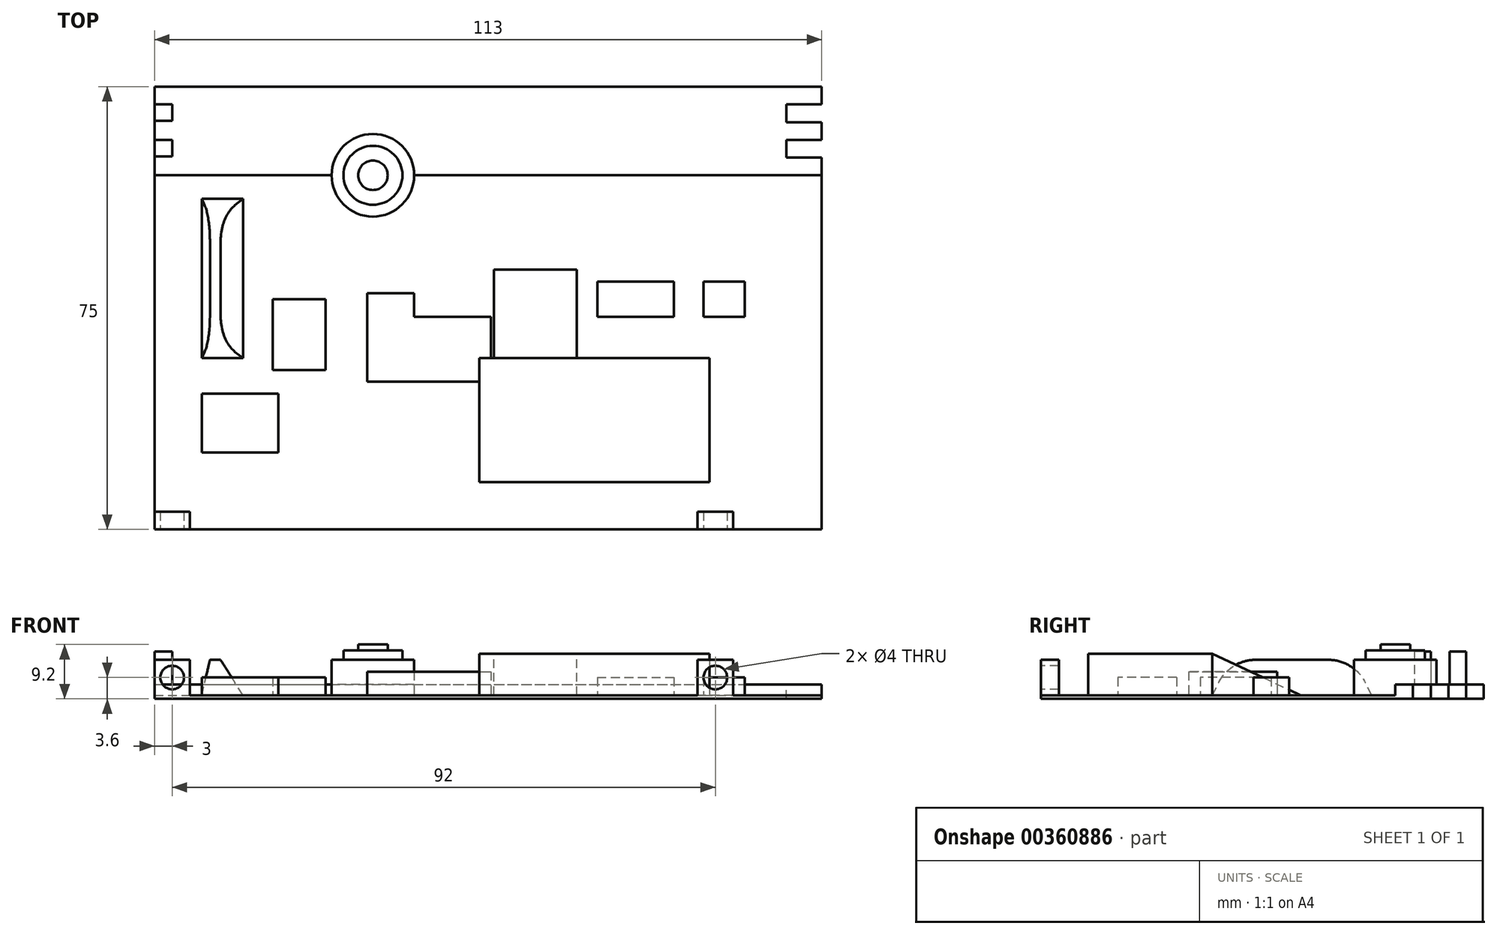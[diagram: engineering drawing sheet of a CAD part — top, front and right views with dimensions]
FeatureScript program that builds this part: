
annotation { "Feature Type Name" : "Feature", "Feature Type Description" : "" }
export const myFeature = defineFeature(function(context is Context, id is Id, definition is map)
    precondition{}
    {
        {
            var Q0;
            Q0=qCreatedBy(makeId("Top.planeOp"),FACE);
            var sketch = newSketch(context, id + "F0", { "sketchPlane" : qUnion([Q0])});
            skLineSegment(sketch, "E0.bottom", {"start": v(-56.5, 75) * mm, "end": v(56.5, 75) * mm});
            skLineSegment(sketch, "E0.top", {"start": v(-56.5, 0) * mm, "end": v(56.5, 0) * mm});
            skLineSegment(sketch, "E0.left", {"start": v(-56.5, 75) * mm, "end": v(-56.5, 0) * mm});
            skLineSegment(sketch, "E0.right", {"start": v(56.5, 75) * mm, "end": v(56.5, 0) * mm});
            skPoint(sketch, "E1", {"position": v(0, 0) * mm});
            skSolve(sketch);
        }
        {
            var Q0;
            Q0 = qSketchRegion(id + "F0", true);
            extrude(context, id + "F1", {"entities" : qUnion([Q0]), "depth" : 0.6 * mm});
        }
        {
            var Q0;
            Q0=makeQuery(id+"F1.opExtrude","CAP_FACE",FACE,{"disambiguationData":[OSD([sQuery(id+"F0.wireOp",EDGE,"E0.bottom"),sQuery(id+"F0.wireOp",EDGE,"E0.top"),sQuery(id+"F0.wireOp",EDGE,"E0.left"),sQuery(id+"F0.wireOp",EDGE,"E0.right")])],"isStart":false});
            var sketch = newSketch(context, id + "F2", { "sketchPlane" : qUnion([Q0])});
            skLineSegment(sketch, "E2.bottom", {"start": v(-56.5, 75) * mm, "end": v(56.5, 75) * mm});
            skLineSegment(sketch, "E2.top", {"start": v(-56.5, 60) * mm, "end": v(56.5, 60) * mm});
            skLineSegment(sketch, "E2.left", {"start": v(-56.5, 75) * mm, "end": v(-56.5, 60) * mm});
            skLineSegment(sketch, "E2.right", {"start": v(56.5, 75) * mm, "end": v(56.5, 60) * mm});
            skSolve(sketch);
        }
        {
            var Q0;
            Q0 = qSketchRegion(id + "F2", true);
            extrude(context, id + "F3", {"entities" : qUnion([Q0]), "operationType" : NewBodyOperationType.ADD, "depth" : 1.8 * mm});
        }
        {
            var Q0;
            Q0=makeQuery(id+"F1.opExtrude","CAP_FACE",FACE,{"disambiguationData":[OSD([sQuery(id+"F0.wireOp",EDGE,"E0.bottom"),sQuery(id+"F0.wireOp",EDGE,"E0.top"),sQuery(id+"F0.wireOp",EDGE,"E0.left"),sQuery(id+"F0.wireOp",EDGE,"E0.right")])],"isStart":false});
            var sketch = newSketch(context, id + "F4", { "sketchPlane" : qUnion([Q0])});
            skCircle(sketch, "E3", {"center": v(-19.5, 60) * mm, "radius": 7 * mm});
            skSolve(sketch);
        }
        {
            var Q0;
            Q0 = qSketchRegion(id + "F4", true);
            extrude(context, id + "F5", {"entities" : qUnion([Q0]), "operationType" : NewBodyOperationType.ADD, "depth" : 6 * mm});
        }
        {
            var Q0;
            Q0=makeQuery(id+"F5.opExtrude","CAP_FACE",FACE,{"disambiguationData":[OSD([sQuery(id+"F4.wireOp",EDGE,"E3")])],"isStart":false});
            var sketch = newSketch(context, id + "F6", { "sketchPlane" : qUnion([Q0])});
            skCircle(sketch, "E4", {"center": v(-19.5, 60) * mm, "radius": 5 * mm});
            skSolve(sketch);
        }
        {
            var Q0;
            Q0 = qSketchRegion(id + "F6", true);
            extrude(context, id + "F7", {"entities" : qUnion([Q0]), "operationType" : NewBodyOperationType.ADD, "depth" : 1.6 * mm});
        }
        {
            var Q0;
            Q0=makeQuery(id+"F7.opExtrude","CAP_FACE",FACE,{"disambiguationData":[OSD([sQuery(id+"F6.wireOp",EDGE,"E4")])],"isStart":false});
            var sketch = newSketch(context, id + "F8", { "sketchPlane" : qUnion([Q0])});
            skCircle(sketch, "E5", {"center": v(-19.5, 60) * mm, "radius": 2.5 * mm});
            skSolve(sketch);
        }
        {
            var Q0;
            Q0 = qSketchRegion(id + "F8", true);
            extrude(context, id + "F9", {"entities" : qUnion([Q0]), "operationType" : NewBodyOperationType.ADD, "depth" : 1 * mm});
        }
        {
            var Q0;
            Q0=makeQuery(id+"F1.opExtrude","CAP_FACE",FACE,{"disambiguationData":[OSD([sQuery(id+"F0.wireOp",EDGE,"E0.bottom"),sQuery(id+"F0.wireOp",EDGE,"E0.top"),sQuery(id+"F0.wireOp",EDGE,"E0.left"),sQuery(id+"F0.wireOp",EDGE,"E0.right")])],"isStart":false});
            var sketch = newSketch(context, id + "F10", { "sketchPlane" : qUnion([Q0])});
            skLineSegment(sketch, "E6.bottom", {"start": v(-48.5, 23) * mm, "end": v(-35.5, 23) * mm});
            skLineSegment(sketch, "E6.top", {"start": v(-48.5, 13) * mm, "end": v(-35.5, 13) * mm});
            skLineSegment(sketch, "E6.left", {"start": v(-48.5, 23) * mm, "end": v(-48.5, 13) * mm});
            skLineSegment(sketch, "E6.right", {"start": v(-35.5, 23) * mm, "end": v(-35.5, 13) * mm});
            skLineSegment(sketch, "E7.bottom", {"start": v(-36.5, 39) * mm, "end": v(-27.5, 39) * mm});
            skLineSegment(sketch, "E7.top", {"start": v(-36.5, 27) * mm, "end": v(-27.5, 27) * mm});
            skLineSegment(sketch, "E7.left", {"start": v(-36.5, 39) * mm, "end": v(-36.5, 27) * mm});
            skLineSegment(sketch, "E7.right", {"start": v(-27.5, 39) * mm, "end": v(-27.5, 27) * mm});
            skLineSegment(sketch, "E8.bottom", {"start": v(18.5, 42) * mm, "end": v(31.5, 42) * mm});
            skLineSegment(sketch, "E8.top", {"start": v(18.5, 36) * mm, "end": v(31.5, 36) * mm});
            skLineSegment(sketch, "E8.left", {"start": v(18.5, 42) * mm, "end": v(18.5, 36) * mm});
            skLineSegment(sketch, "E8.right", {"start": v(31.5, 42) * mm, "end": v(31.5, 36) * mm});
            skLineSegment(sketch, "E9.bottom", {"start": v(36.5, 42) * mm, "end": v(43.5, 42) * mm});
            skLineSegment(sketch, "E9.top", {"start": v(36.5, 36) * mm, "end": v(43.5, 36) * mm});
            skLineSegment(sketch, "E9.left", {"start": v(36.5, 42) * mm, "end": v(36.5, 36) * mm});
            skLineSegment(sketch, "E9.right", {"start": v(43.5, 42) * mm, "end": v(43.5, 36) * mm});
            skSolve(sketch);
        }
        {
            var Q0;
            Q0 = qSketchRegion(id + "F10", true);
            extrude(context, id + "F11", {"entities" : qUnion([Q0]), "operationType" : NewBodyOperationType.ADD, "depth" : 3 * mm});
        }
        {
            var Q0;
            Q0=makeQuery(id+"F1.opExtrude","CAP_FACE",FACE,{"disambiguationData":[OSD([sQuery(id+"F0.wireOp",EDGE,"E0.bottom"),sQuery(id+"F0.wireOp",EDGE,"E0.top"),sQuery(id+"F0.wireOp",EDGE,"E0.left"),sQuery(id+"F0.wireOp",EDGE,"E0.right")])],"isStart":false});
            var sketch = newSketch(context, id + "F12", { "sketchPlane" : qUnion([Q0])});
            skLineSegment(sketch, "E10", {"start": v(-20.5, 40) * mm, "end": v(-12.5, 40) * mm});
            skLineSegment(sketch, "E11", {"start": v(-12.5, 40) * mm, "end": v(-12.5, 36) * mm});
            skLineSegment(sketch, "E12", {"start": v(-12.5, 36) * mm, "end": v(0.5, 36) * mm});
            skLineSegment(sketch, "E13", {"start": v(0.5, 36) * mm, "end": v(0.5, 25) * mm});
            skLineSegment(sketch, "E14", {"start": v(0.5, 25) * mm, "end": v(-20.5, 25) * mm});
            skLineSegment(sketch, "E15", {"start": v(-20.5, 25) * mm, "end": v(-20.5, 40) * mm});
            skSolve(sketch);
        }
        {
            var Q0;
            Q0=makeQuery(id+"F1.opExtrude","CAP_FACE",FACE,{"disambiguationData":[OSD([sQuery(id+"F0.wireOp",EDGE,"E0.bottom"),sQuery(id+"F0.wireOp",EDGE,"E0.top"),sQuery(id+"F0.wireOp",EDGE,"E0.left"),sQuery(id+"F0.wireOp",EDGE,"E0.right")])],"isStart":false});
            var sketch = newSketch(context, id + "F13", { "sketchPlane" : qUnion([Q0])});
            skLineSegment(sketch, "E16.bottom", {"start": v(-1.5, 29) * mm, "end": v(37.5, 29) * mm});
            skLineSegment(sketch, "E16.top", {"start": v(-1.5, 8) * mm, "end": v(37.5, 8) * mm});
            skLineSegment(sketch, "E16.left", {"start": v(-1.5, 29) * mm, "end": v(-1.5, 8) * mm});
            skLineSegment(sketch, "E16.right", {"start": v(37.5, 29) * mm, "end": v(37.5, 8) * mm});
            skSolve(sketch);
        }
        {
            var Q0;
            Q0 = qSketchRegion(id + "F13", true);
            extrude(context, id + "F14", {"entities" : qUnion([Q0]), "operationType" : NewBodyOperationType.ADD, "depth" : 7 * mm});
        }
        {
            var Q0;
            Q0 = qSketchRegion(id + "F12", true);
            extrude(context, id + "F15", {"entities" : qUnion([Q0]), "operationType" : NewBodyOperationType.ADD, "depth" : 4 * mm});
        }
        {
            var Q0;
            Q0=qCreatedBy(makeId("Right.planeOp"),FACE);
            cPlane(context, id + "F16", {"entities" : qUnion([Q0]), "cplaneType" : CPlaneType.OFFSET, "offset" : 15 * mm, "width" : 150 * mm, "height" : 150 * mm});
        }
        {
            var Q0;
            Q0=qCreatedBy(id+"F16.planeOp",FACE);
            var sketch = newSketch(context, id + "F17", { "sketchPlane" : qUnion([Q0])});
            skLineSegment(sketch, "E17", {"start": v(44, 0.6) * mm, "end": v(29, 0.6) * mm});
            skLineSegment(sketch, "E18", {"start": v(29, 0.6) * mm, "end": v(29, 7.6) * mm});
            skLineSegment(sketch, "E19", {"start": v(29, 7.6) * mm, "end": v(44, 0.6) * mm});
            skSolve(sketch);
        }
        {
            var Q0;
            Q0 = qSketchRegion(id + "F17", true);
            extrude(context, id + "F18", {"entities" : qUnion([Q0]), "operationType" : NewBodyOperationType.ADD, "oppositeDirection" : true, "depth" : 14 * mm});
        }
        {
            var Q0;
            Q0=makeQuery(id+"F1.opExtrude","CAP_FACE",FACE,{"disambiguationData":[OSD([sQuery(id+"F0.wireOp",EDGE,"E0.bottom"),sQuery(id+"F0.wireOp",EDGE,"E0.top"),sQuery(id+"F0.wireOp",EDGE,"E0.left"),sQuery(id+"F0.wireOp",EDGE,"E0.right")])],"isStart":false});
            var sketch = newSketch(context, id + "F19", { "sketchPlane" : qUnion([Q0])});
            skLineSegment(sketch, "E20.bottom", {"start": v(-48.5, 56) * mm, "end": v(-41.5, 56) * mm});
            skLineSegment(sketch, "E20.top", {"start": v(-48.5, 29) * mm, "end": v(-41.5, 29) * mm});
            skLineSegment(sketch, "E20.left", {"start": v(-48.5, 56) * mm, "end": v(-48.5, 29) * mm});
            skLineSegment(sketch, "E20.right", {"start": v(-41.5, 56) * mm, "end": v(-41.5, 29) * mm});
            skSolve(sketch);
        }
        {
            var Q0;
            Q0=makeQuery(id+"F19.imprint","IMPRINT",FACE,{"disambiguationData":[TD([[makeQuery(id+"F19.imprint","IMPRINT",EDGE,{"derivedFrom":sQuery(id+"F19.wireOp",EDGE,"E20.bottom")}),-1.0]])]});
            cPlane(context, id + "F20", {"entities" : qUnion([Q0]), "cplaneType" : CPlaneType.OFFSET, "offset" : 6 * mm, "width" : 150 * mm, "height" : 150 * mm});
        }
        {
            var Q0;
            Q0=qCreatedBy(id+"F20.planeOp",FACE);
            var sketch = newSketch(context, id + "F21", { "sketchPlane" : qUnion([Q0])});
            skLineSegment(sketch, "E21.bottom", {"start": v(-47.1, 53) * mm, "end": v(-45.3, 53) * mm});
            skLineSegment(sketch, "E21.top", {"start": v(-47.1, 32) * mm, "end": v(-45.3, 32) * mm});
            skLineSegment(sketch, "E21.left", {"start": v(-47.1, 53) * mm, "end": v(-47.1, 32) * mm});
            skLineSegment(sketch, "E21.right", {"start": v(-45.3, 53) * mm, "end": v(-45.3, 32) * mm});
            skSolve(sketch);
        }
        {
            var Q1;
            Q1=makeQuery(id+"F19.imprint","IMPRINT",FACE,{"disambiguationData":[TD([[makeQuery(id+"F19.imprint","IMPRINT",EDGE,{"derivedFrom":sQuery(id+"F19.wireOp",EDGE,"E20.bottom")}),-1.0]])]});
            var Q2;
            Q2=makeQuery(id+"F21.imprint","IMPRINT",FACE,{"disambiguationData":[TD([[makeQuery(id+"F21.imprint","IMPRINT",EDGE,{"derivedFrom":sQuery(id+"F21.wireOp",EDGE,"E21.bottom")}),-1.0]])]});
            loft(context, id + "F22", {"operationType" : NewBodyOperationType.ADD, "sheetProfilesArray" : [{ "sheetProfileEntities" : qUnion([Q1]) }, { "sheetProfileEntities" : qUnion([Q2]) }]});
        }
        {
            var Q0;
            Q0=makeQuery(id+"F22.opLoft","MID_CAP_EDGE",EDGE,{"disambiguationData":[OSD([sQuery(id+"F21.wireOp",EDGE,"E21.bottom"),sQuery(id+"F21.wireOp",EDGE,"E21.left"),sQuery(id+"F21.wireOp",EDGE,"E21.right")])],"capPos":1.0});
            var Q1;
            Q1=makeQuery(id+"F22.opLoft","MID_CAP_EDGE",EDGE,{"disambiguationData":[OSD([sQuery(id+"F21.wireOp",EDGE,"E21.top"),sQuery(id+"F21.wireOp",EDGE,"E21.left"),sQuery(id+"F21.wireOp",EDGE,"E21.right")])],"capPos":1.0});
            fillet(context, id + "F23", {"entities" : qUnion([Q0, Q1]), "radius" : 7 * mm, "tangentPropagation" : true, "allowEdgeOverflow" : false});
        }
        {
            var Q0;
            Q0=makeQuery(id+"F3.opExtrude","CAP_FACE",FACE,{"disambiguationData":[OSD([sQuery(id+"F2.wireOp",EDGE,"E2.bottom"),sQuery(id+"F2.wireOp",EDGE,"E2.top"),sQuery(id+"F2.wireOp",EDGE,"E2.left"),sQuery(id+"F2.wireOp",EDGE,"E2.right")])],"isStart":false});
            var sketch = newSketch(context, id + "F24", { "sketchPlane" : qUnion([Q0])});
            skLineSegment(sketch, "E22.bottom", {"start": v(-56.5, 72) * mm, "end": v(-53.5, 72) * mm});
            skLineSegment(sketch, "E22.top", {"start": v(-56.5, 69.2) * mm, "end": v(-53.5, 69.2) * mm});
            skLineSegment(sketch, "E22.left", {"start": v(-56.5, 72) * mm, "end": v(-56.5, 69.2) * mm});
            skLineSegment(sketch, "E22.right", {"start": v(-53.5, 72) * mm, "end": v(-53.5, 69.2) * mm});
            skLineSegment(sketch, "E23.bottom", {"start": v(-56.5, 66) * mm, "end": v(-53.5, 66) * mm});
            skLineSegment(sketch, "E23.top", {"start": v(-56.5, 63.2) * mm, "end": v(-53.5, 63.2) * mm});
            skLineSegment(sketch, "E23.left", {"start": v(-56.5, 66) * mm, "end": v(-56.5, 63.2) * mm});
            skLineSegment(sketch, "E23.right", {"start": v(-53.5, 66) * mm, "end": v(-53.5, 63.2) * mm});
            skSolve(sketch);
        }
        {
            var Q0;
            Q0 = qSketchRegion(id + "F24", true);
            extrude(context, id + "F25", {"entities" : qUnion([Q0]), "operationType" : NewBodyOperationType.ADD, "depth" : 5.6 * mm});
        }
        {
            var Q0;
            Q0=makeQuery(id+"F3.opExtrude","CAP_FACE",FACE,{"disambiguationData":[OSD([sQuery(id+"F2.wireOp",EDGE,"E2.bottom"),sQuery(id+"F2.wireOp",EDGE,"E2.top"),sQuery(id+"F2.wireOp",EDGE,"E2.left"),sQuery(id+"F2.wireOp",EDGE,"E2.right")])],"isStart":false});
            var sketch = newSketch(context, id + "F26", { "sketchPlane" : qUnion([Q0])});
            skLineSegment(sketch, "E24.bottom", {"start": v(50.5, 72) * mm, "end": v(56.5, 72) * mm});
            skLineSegment(sketch, "E24.top", {"start": v(50.5, 69) * mm, "end": v(56.5, 69) * mm});
            skLineSegment(sketch, "E24.left", {"start": v(50.5, 72) * mm, "end": v(50.5, 69) * mm});
            skLineSegment(sketch, "E24.right", {"start": v(56.5, 72) * mm, "end": v(56.5, 69) * mm});
            skLineSegment(sketch, "E25.bottom", {"start": v(50.5, 66) * mm, "end": v(56.5, 66) * mm});
            skLineSegment(sketch, "E25.top", {"start": v(50.5, 63) * mm, "end": v(56.5, 63) * mm});
            skLineSegment(sketch, "E25.left", {"start": v(50.5, 66) * mm, "end": v(50.5, 63) * mm});
            skLineSegment(sketch, "E25.right", {"start": v(56.5, 66) * mm, "end": v(56.5, 63) * mm});
            skSolve(sketch);
        }
        {
            var Q0;
            Q0 = qSketchRegion(id + "F26", true);
            extrude(context, id + "F27", {"entities" : qUnion([Q0]), "operationType" : NewBodyOperationType.REMOVE, "oppositeDirection" : true, "depth" : 3 * mm});
        }
        {
            var Q0;
            Q0=makeQuery(id+"F1.opExtrude","CAP_FACE",FACE,{"disambiguationData":[OSD([sQuery(id+"F0.wireOp",EDGE,"E0.bottom"),sQuery(id+"F0.wireOp",EDGE,"E0.top"),sQuery(id+"F0.wireOp",EDGE,"E0.left"),sQuery(id+"F0.wireOp",EDGE,"E0.right")])],"isStart":false});
            var sketch = newSketch(context, id + "F28", { "sketchPlane" : qUnion([Q0])});
            skLineSegment(sketch, "E26.bottom", {"start": v(-56.5, 0) * mm, "end": v(-50.5, 0) * mm});
            skLineSegment(sketch, "E26.top", {"start": v(-56.5, 3) * mm, "end": v(-50.5, 3) * mm});
            skLineSegment(sketch, "E26.left", {"start": v(-56.5, 0) * mm, "end": v(-56.5, 3) * mm});
            skLineSegment(sketch, "E26.right", {"start": v(-50.5, 0) * mm, "end": v(-50.5, 3) * mm});
            skLineSegment(sketch, "E27.bottom", {"start": v(41.5, 0) * mm, "end": v(35.5, 0) * mm});
            skLineSegment(sketch, "E27.top", {"start": v(41.5, 3) * mm, "end": v(35.5, 3) * mm});
            skLineSegment(sketch, "E27.left", {"start": v(41.5, 0) * mm, "end": v(41.5, 3) * mm});
            skLineSegment(sketch, "E27.right", {"start": v(35.5, 0) * mm, "end": v(35.5, 3) * mm});
            skSolve(sketch);
        }
        {
            var Q0;
            Q0 = qSketchRegion(id + "F28", true);
            extrude(context, id + "F29", {"entities" : qUnion([Q0]), "operationType" : NewBodyOperationType.ADD, "depth" : 6 * mm});
        }
        {
            var Q0;
            Q0=makeQuery(id+"F29.boolean.opBoolean","MERGE",FACE,{"derivedFrom":[makeQuery(id+"F1.opExtrude","SWEPT_FACE",FACE,{"disambiguationData":[OSD([sQuery(id+"F0.wireOp",EDGE,"E0.top")])]}),makeQuery(id+"F29.opExtrude","SWEPT_FACE",FACE,{"disambiguationData":[OSD([sQuery(id+"F28.wireOp",EDGE,"E26.bottom")])]}),makeQuery(id+"F29.opExtrude","SWEPT_FACE",FACE,{"disambiguationData":[OSD([sQuery(id+"F28.wireOp",EDGE,"E27.bottom")])]})]});
            var sketch = newSketch(context, id + "F30", { "sketchPlane" : qUnion([Q0])});
            skCircle(sketch, "E28", {"center": v(-53.5, 3.6) * mm, "radius": 2 * mm});
            skCircle(sketch, "E29", {"center": v(38.5, 3.6) * mm, "radius": 2 * mm});
            skSolve(sketch);
        }
        {
            var Q0;
            Q0 = qSketchRegion(id + "F30", true);
            extrude(context, id + "F31", {"entities" : qUnion([Q0]), "operationType" : NewBodyOperationType.REMOVE, "oppositeDirection" : true, "depth" : 4 * mm});
        }
    });
